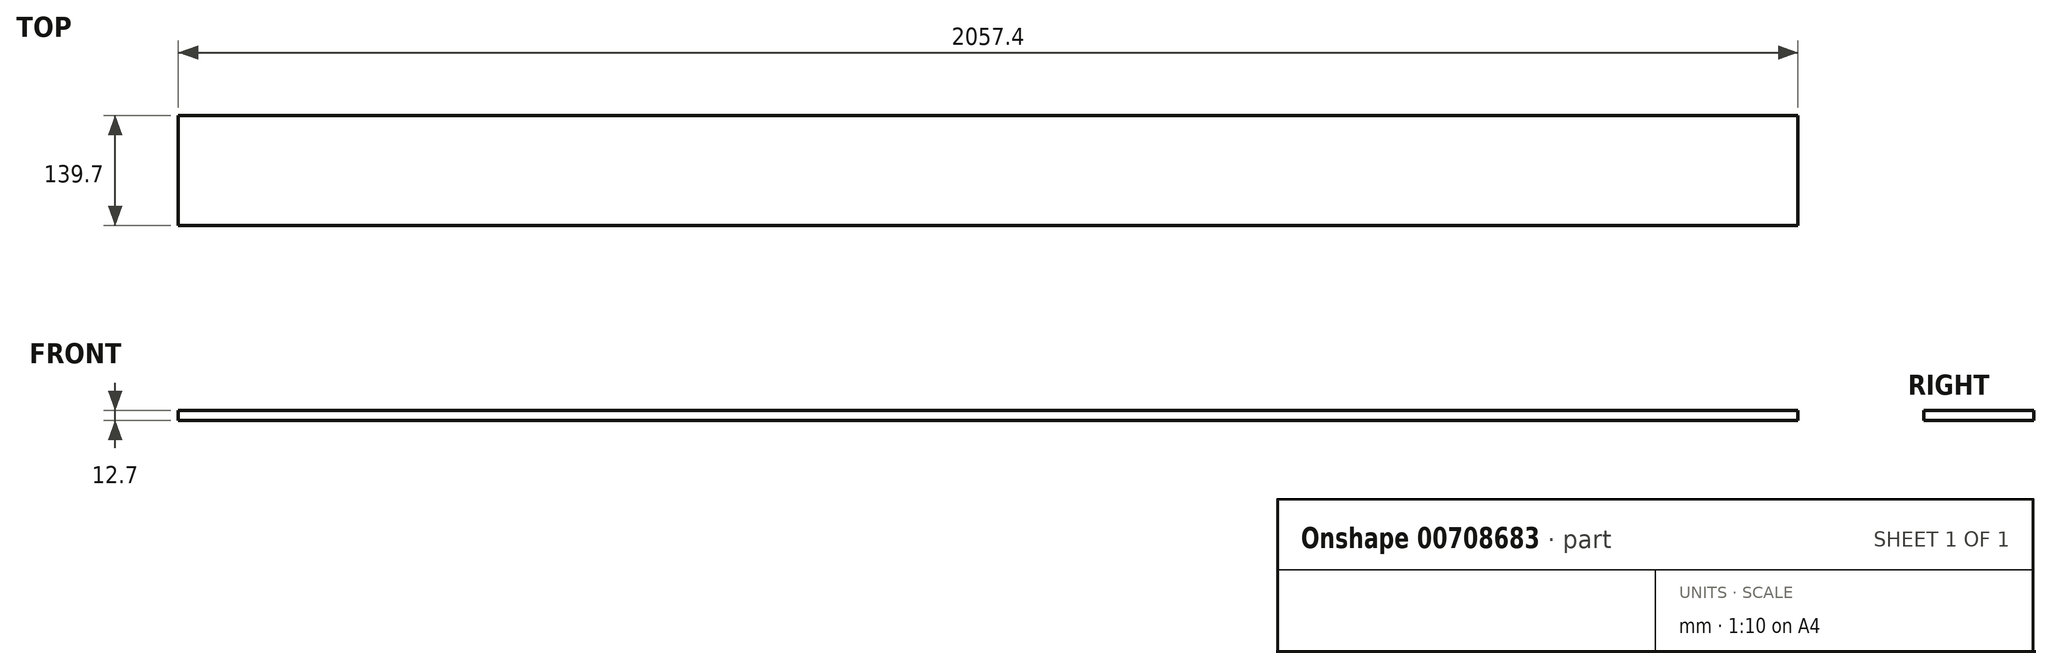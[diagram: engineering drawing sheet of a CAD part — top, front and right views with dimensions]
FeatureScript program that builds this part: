
annotation { "Feature Type Name" : "Feature", "Feature Type Description" : "" }
export const myFeature = defineFeature(function(context is Context, id is Id, definition is map)
    precondition{}
    {
        {
            var Q0;
            Q0=qCreatedBy(makeId("Top.planeOp"),FACE);
            var sketch = newSketch(context, id + "F0", { "sketchPlane" : qUnion([Q0])});
            skLineSegment(sketch, "E0.bottom", {"start": v(1028.7, 69.85) * mm, "end": v(-1028.7, 69.85) * mm});
            skLineSegment(sketch, "E0.top", {"start": v(1028.7, -69.85) * mm, "end": v(-1028.7, -69.85) * mm});
            skLineSegment(sketch, "E0.left", {"start": v(1028.7, 69.85) * mm, "end": v(1028.7, -69.85) * mm});
            skLineSegment(sketch, "E0.right", {"start": v(-1028.7, 69.85) * mm, "end": v(-1028.7, -69.85) * mm});
            skPoint(sketch, "E0.middle", {"position": v(0, 0) * mm});
            skSolve(sketch);
        }
        {
            var Q0;
            Q0=makeQuery(id+"F0.imprint","IMPRINT",FACE,{"disambiguationData":[TD([[makeQuery(id+"F0.imprint","IMPRINT",EDGE,{"derivedFrom":sQuery(id+"F0.wireOp",EDGE,"E0.bottom")}),1.0]])]});
            extrude(context, id + "F1", {"entities" : qUnion([Q0]), "depth" : 12.7 * mm, "offsetDistance" : 25.4 * mm});
        }
    });
